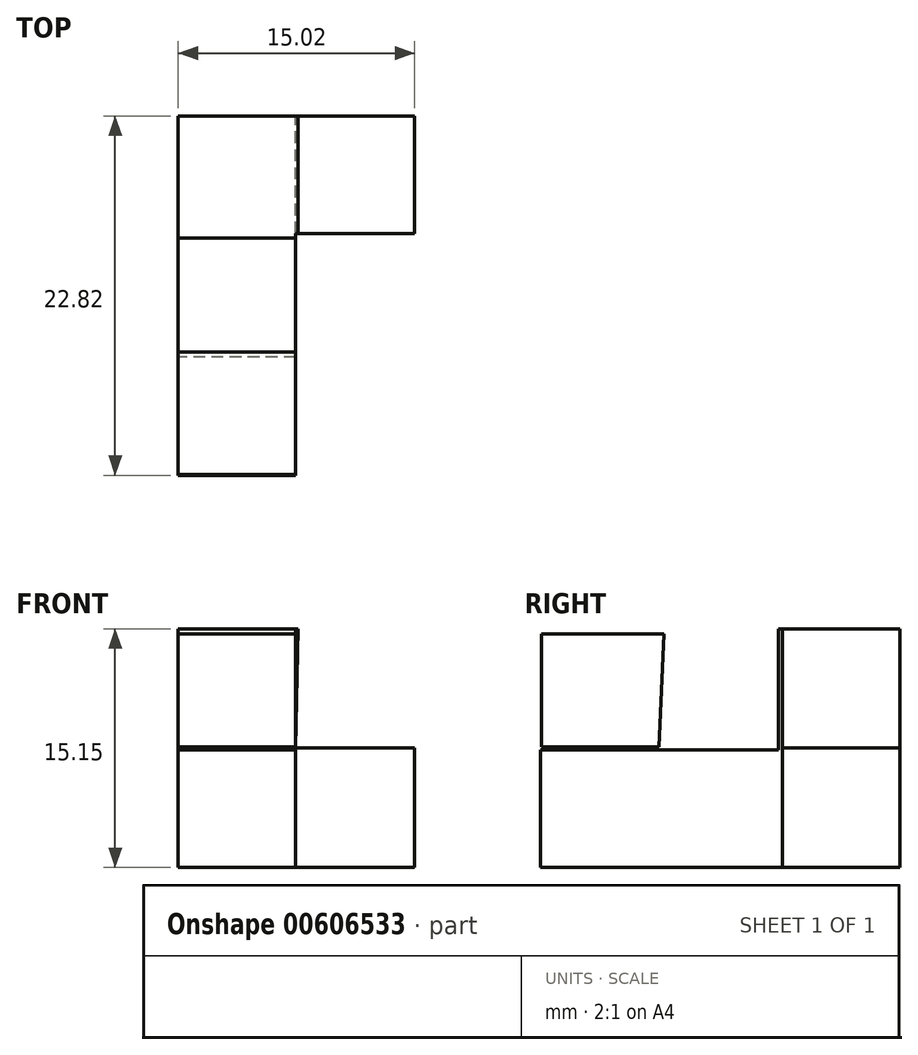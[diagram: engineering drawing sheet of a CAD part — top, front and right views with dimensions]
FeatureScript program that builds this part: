
annotation { "Feature Type Name" : "Feature", "Feature Type Description" : "" }
export const myFeature = defineFeature(function(context is Context, id is Id, definition is map)
    precondition{}
    {
        {
            var Q0;
            Q0=qCreatedBy(makeId("Front.planeOp"),FACE);
            var sketch = newSketch(context, id + "F0", { "sketchPlane" : qUnion([Q0])});
            skLineSegment(sketch, "E0", {"start": v(0, 15.15) * mm, "end": v(0, 0) * mm});
            skLineSegment(sketch, "E1", {"start": v(0, 0) * mm, "end": v(15.02, 0) * mm});
            skLineSegment(sketch, "E2", {"start": v(15.02, 0) * mm, "end": v(15.02, 7.58) * mm});
            skPoint(sketch, "E2.endSnap0", {"position": v(0, 7.58) * mm});
            skLineSegment(sketch, "E3", {"start": v(15.02, 7.58) * mm, "end": v(7.46, 7.58) * mm});
            skLineSegment(sketch, "E4", {"start": v(0, 15.15) * mm, "end": v(7.62, 15.15) * mm});
            skLineSegment(sketch, "E5", {"start": v(7.62, 15.15) * mm, "end": v(7.46, 7.58) * mm});
            skSolve(sketch);
        }
        {
            var Q0;
            Q0 = qSketchRegion(id + "F0", true);
            extrude(context, id + "F1", {"entities" : qUnion([Q0]), "depth" : 7.46 * mm, "offsetDistance" : 25.4 * mm});
        }
        {
            var Q0;
            Q0=qCreatedBy(makeId("Right.planeOp"),FACE);
            var sketch = newSketch(context, id + "F2", { "sketchPlane" : qUnion([Q0])});
            skLineSegment(sketch, "E6", {"start": v(0, 12.43) * mm, "end": v(0, 0) * mm});
            skLineSegment(sketch, "E7", {"start": v(0, 0) * mm, "end": v(-15.3, 0) * mm});
            skLineSegment(sketch, "E8", {"start": v(-15.3, 0) * mm, "end": v(-15.3, 7.46) * mm});
            skLineSegment(sketch, "E9", {"start": v(-15.3, 7.46) * mm, "end": v(-7.73, 7.46) * mm});
            skLineSegment(sketch, "E10", {"start": v(-7.73, 7.46) * mm, "end": v(-7.73, 15.15) * mm});
            skLineSegment(sketch, "E11", {"start": v(-7.73, 15.15) * mm, "end": v(0, 15.15) * mm});
            skLineSegment(sketch, "E12", {"start": v(0, 15.15) * mm, "end": v(0, 12.43) * mm});
            skSolve(sketch);
        }
        {
            var Q0;
            Q0 = qSketchRegion(id + "F2", true);
            extrude(context, id + "F3", {"entities" : qUnion([Q0]), "operationType" : NewBodyOperationType.ADD, "depth" : 7.46 * mm, "offsetDistance" : 25.4 * mm});
        }
        {
            var Q0;
            Q0=qCreatedBy(makeId("Right.planeOp"),FACE);
            var sketch = newSketch(context, id + "F4", { "sketchPlane" : qUnion([Q0])});
            skLineSegment(sketch, "E13", {"start": v(-15.19, 0) * mm, "end": v(-22.82, 0) * mm});
            skLineSegment(sketch, "E14", {"start": v(-15.29, 7.46) * mm, "end": v(-22.82, 7.46) * mm});
            skLineSegment(sketch, "E15", {"start": v(-22.82, 7.46) * mm, "end": v(-22.82, 0) * mm});
            skLineSegment(sketch, "E16", {"start": v(-15.29, 7.46) * mm, "end": v(-15.19, 0) * mm});
            skSolve(sketch);
        }
        {
            var Q0;
            Q0 = qSketchRegion(id + "F4", true);
            extrude(context, id + "F5", {"entities" : qUnion([Q0]), "operationType" : NewBodyOperationType.ADD, "depth" : 7.46 * mm, "offsetDistance" : 25.4 * mm});
        }
        {
            var Q0;
            Q0=qCreatedBy(makeId("Right.planeOp"),FACE);
            var sketch = newSketch(context, id + "F6", { "sketchPlane" : qUnion([Q0])});
            skLineSegment(sketch, "E17", {"start": v(-22.76, 7.66) * mm, "end": v(-15.3, 7.66) * mm});
            skLineSegment(sketch, "E18", {"start": v(-22.76, 7.66) * mm, "end": v(-22.76, 14.84) * mm});
            skLineSegment(sketch, "E19", {"start": v(-22.76, 14.84) * mm, "end": v(-14.99, 14.84) * mm});
            skLineSegment(sketch, "E20", {"start": v(-14.99, 14.84) * mm, "end": v(-15.3, 7.66) * mm});
            skSolve(sketch);
        }
        {
            var Q0;
            Q0 = qSketchRegion(id + "F6", true);
            extrude(context, id + "F7", {"entities" : qUnion([Q0]), "depth" : 7.46 * mm, "offsetDistance" : 25.4 * mm});
        }
    });
